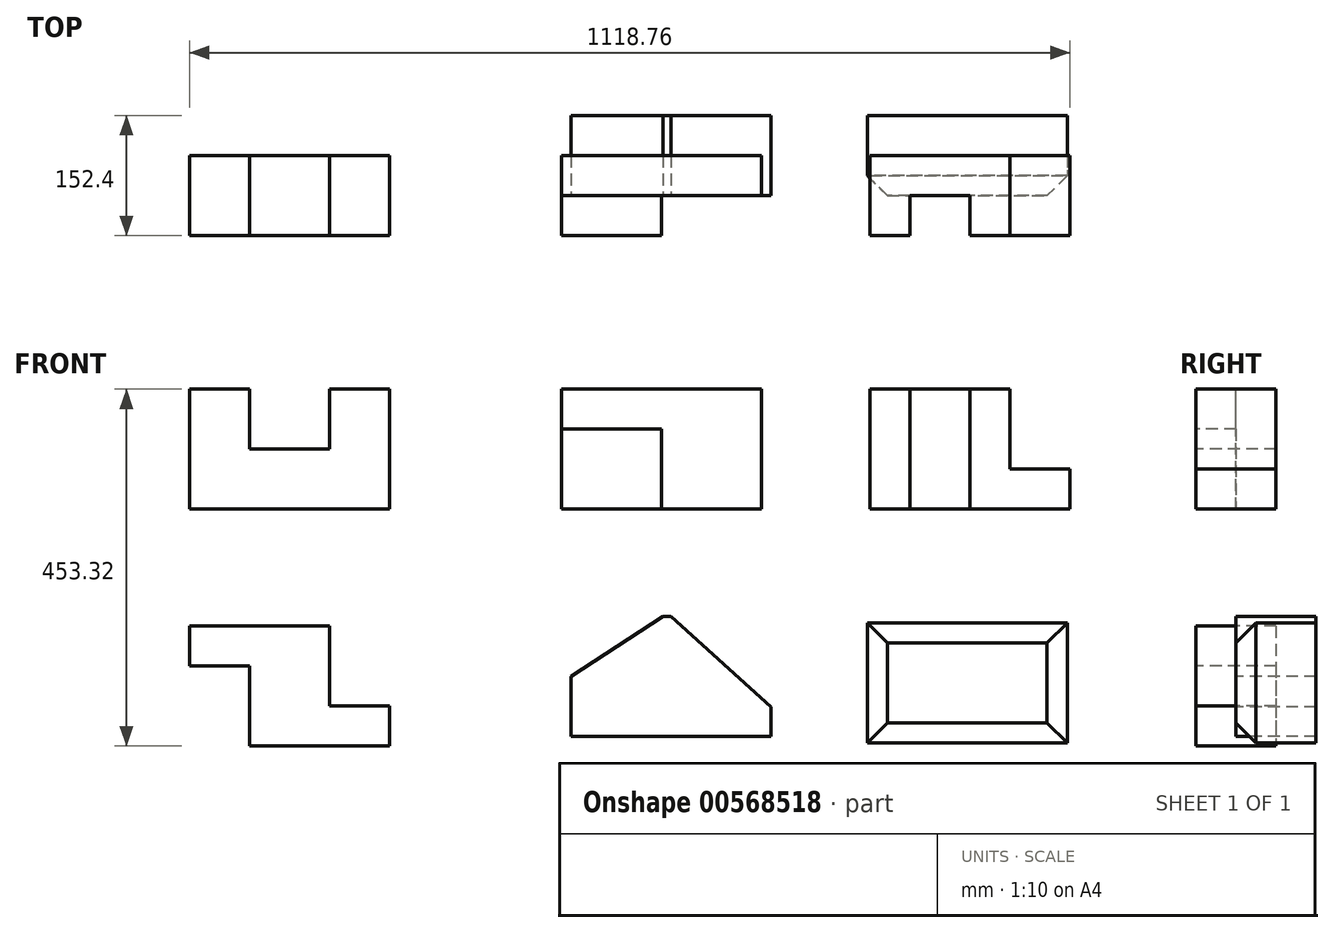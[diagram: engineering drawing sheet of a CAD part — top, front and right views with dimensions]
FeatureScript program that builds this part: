
annotation { "Feature Type Name" : "Feature", "Feature Type Description" : "" }
export const myFeature = defineFeature(function(context is Context, id is Id, definition is map)
    precondition{}
    {
        {
            var Q0;
            Q0=qCreatedBy(makeId("Front.planeOp"),FACE);
            var sketch = newSketch(context, id + "F0", { "sketchPlane" : qUnion([Q0])});
            skLineSegment(sketch, "E0", {"start": v(0, 0) * mm, "end": v(254, 0) * mm});
            skLineSegment(sketch, "E1", {"start": v(254, 0) * mm, "end": v(254, 152.4) * mm});
            skLineSegment(sketch, "E2", {"start": v(254, 152.4) * mm, "end": v(177.8, 152.4) * mm});
            skLineSegment(sketch, "E3", {"start": v(177.8, 152.4) * mm, "end": v(177.8, 76.2) * mm});
            skLineSegment(sketch, "E4", {"start": v(177.8, 76.2) * mm, "end": v(76.2, 76.2) * mm});
            skLineSegment(sketch, "E5", {"start": v(76.2, 76.2) * mm, "end": v(76.2, 152.4) * mm});
            skLineSegment(sketch, "E6", {"start": v(76.2, 152.4) * mm, "end": v(0, 152.4) * mm});
            skLineSegment(sketch, "E7", {"start": v(0, 152.4) * mm, "end": v(0, 0) * mm});
            skSolve(sketch);
        }
        {
            var Q0;
            Q0=makeQuery(id+"F0.imprint","IMPRINT",FACE,{"disambiguationData":[TD([[makeQuery(id+"F0.imprint","IMPRINT",EDGE,{"derivedFrom":sQuery(id+"F0.wireOp",EDGE,"E0")}),1.0]])]});
            extrude(context, id + "F1", {"entities" : qUnion([Q0]), "oppositeDirection" : true, "depth" : 101.6 * mm, "offsetDistance" : 25.4 * mm});
        }
        {
            var Q0;
            Q0=qCreatedBy(makeId("Front.planeOp"),FACE);
            var sketch = newSketch(context, id + "F2", { "sketchPlane" : qUnion([Q0])});
            skLineSegment(sketch, "E8.bottom", {"start": v(472.59, 0) * mm, "end": v(726.59, 0) * mm});
            skLineSegment(sketch, "E8.top", {"start": v(472.59, 152.4) * mm, "end": v(726.59, 152.4) * mm});
            skLineSegment(sketch, "E8.left", {"start": v(472.59, 0) * mm, "end": v(472.59, 152.4) * mm});
            skLineSegment(sketch, "E8.right", {"start": v(726.59, 0) * mm, "end": v(726.59, 152.4) * mm});
            skSolve(sketch);
        }
        {
            var Q0;
            Q0=makeQuery(id+"F2.imprint","IMPRINT",FACE,{"disambiguationData":[TD([[makeQuery(id+"F2.imprint","IMPRINT",EDGE,{"derivedFrom":sQuery(id+"F2.wireOp",EDGE,"E8.bottom")}),1.0]])]});
            extrude(context, id + "F3", {"entities" : qUnion([Q0]), "oppositeDirection" : true, "depth" : 101.6 * mm, "offsetDistance" : 25.4 * mm});
        }
        {
            var Q0;
            Q0=makeQuery(id+"F3.opExtrude","CAP_FACE",FACE,{"disambiguationData":[OSD([sQuery(id+"F2.wireOp",EDGE,"E8.bottom"),sQuery(id+"F2.wireOp",EDGE,"E8.top"),sQuery(id+"F2.wireOp",EDGE,"E8.left"),sQuery(id+"F2.wireOp",EDGE,"E8.right")])],"isStart":true});
            var sketch = newSketch(context, id + "F4", { "sketchPlane" : qUnion([Q0])});
            skLineSegment(sketch, "E9", {"start": v(472.59, 152.4) * mm, "end": v(472.59, 101.6) * mm});
            skLineSegment(sketch, "E10", {"start": v(472.59, 101.6) * mm, "end": v(599.59, 101.6) * mm});
            skLineSegment(sketch, "E11", {"start": v(599.59, 101.6) * mm, "end": v(599.59, 0) * mm});
            skLineSegment(sketch, "E12", {"start": v(472.59, 152.4) * mm, "end": v(726.59, 152.4) * mm});
            skLineSegment(sketch, "E13", {"start": v(726.59, 152.4) * mm, "end": v(726.59, 0) * mm});
            skLineSegment(sketch, "E14", {"start": v(726.59, 0) * mm, "end": v(599.59, 0) * mm});
            skSolve(sketch);
        }
        {
            var Q0;
            Q0=makeQuery(id+"F4.imprint","IMPRINT",FACE,{"disambiguationData":[TD([[makeQuery(id+"F4.imprint","IMPRINT",EDGE,{"derivedFrom":sQuery(id+"F4.wireOp",EDGE,"E9")}),-1.0]])]});
            extrude(context, id + "F5", {"entities" : qUnion([Q0]), "operationType" : NewBodyOperationType.REMOVE, "oppositeDirection" : true, "depth" : 50.8 * mm, "offsetDistance" : 25.4 * mm});
        }
        {
            var Q0;
            Q0=qCreatedBy(makeId("Front.planeOp"),FACE);
            var sketch = newSketch(context, id + "F6", { "sketchPlane" : qUnion([Q0])});
            skLineSegment(sketch, "E15.bottom", {"start": v(864.76, 0) * mm, "end": v(1118.76, 0) * mm});
            skLineSegment(sketch, "E15.top", {"start": v(864.76, 152.4) * mm, "end": v(1118.76, 152.4) * mm});
            skLineSegment(sketch, "E15.left", {"start": v(864.76, 0) * mm, "end": v(864.76, 152.4) * mm});
            skLineSegment(sketch, "E15.right", {"start": v(1118.76, 0) * mm, "end": v(1118.76, 152.4) * mm});
            skSolve(sketch);
        }
        {
            var Q0;
            Q0=makeQuery(id+"F6.imprint","IMPRINT",FACE,{"disambiguationData":[TD([[makeQuery(id+"F6.imprint","IMPRINT",EDGE,{"derivedFrom":sQuery(id+"F6.wireOp",EDGE,"E15.bottom")}),1.0]])]});
            extrude(context, id + "F7", {"entities" : qUnion([Q0]), "oppositeDirection" : true, "depth" : 101.6 * mm, "offsetDistance" : 25.4 * mm});
        }
        {
            var Q0;
            Q0=makeQuery(id+"F7.opExtrude","SWEPT_FACE",FACE,{"disambiguationData":[OSD([sQuery(id+"F6.wireOp",EDGE,"E15.top")])]});
            var sketch = newSketch(context, id + "F8", { "sketchPlane" : qUnion([Q0])});
            skLineSegment(sketch, "E16.bottom", {"start": v(915.56, 0) * mm, "end": v(991.76, 0) * mm});
            skLineSegment(sketch, "E16.top", {"start": v(915.56, 50.8) * mm, "end": v(991.76, 50.8) * mm});
            skLineSegment(sketch, "E16.left", {"start": v(915.56, 0) * mm, "end": v(915.56, 50.8) * mm});
            skLineSegment(sketch, "E16.right", {"start": v(991.76, 0) * mm, "end": v(991.76, 50.8) * mm});
            skSolve(sketch);
        }
        {
            var Q0;
            Q0=makeQuery(id+"F8.imprint","IMPRINT",FACE,{"disambiguationData":[TD([[makeQuery(id+"F8.imprint","IMPRINT",EDGE,{"derivedFrom":sQuery(id+"F8.wireOp",EDGE,"E16.bottom")}),1.0]])]});
            extrude(context, id + "F9", {"entities" : qUnion([Q0]), "operationType" : NewBodyOperationType.REMOVE, "oppositeDirection" : true, "depth" : 152.4 * mm, "offsetDistance" : 25.4 * mm});
        }
        {
            var Q0;
            {var subQ0=sQuery(id+"F6.wireOp",EDGE,"E15.bottom");var subQ1=sQuery(id+"F6.wireOp",EDGE,"E15.right");var subQ2=sQuery(id+"F6.wireOp",EDGE,"E15.top");Q0=makeQuery(id+"F9.boolean.opBoolean","SPLIT",FACE,{"disambiguationData":[TD([makeQuery(id+"F7.opExtrude","SWEPT_FACE",FACE,{"disambiguationData":[OSD([subQ1])]})])],"derivedFrom":makeQuery(id+"F7.opExtrude","CAP_FACE",FACE,{"disambiguationData":[OSD([subQ0,subQ2,sQuery(id+"F6.wireOp",EDGE,"E15.left"),subQ1])],"isStart":true})});}
            var sketch = newSketch(context, id + "F10", { "sketchPlane" : qUnion([Q0])});
            skLineSegment(sketch, "E17.bottom", {"start": v(1042.56, 152.4) * mm, "end": v(1118.76, 152.4) * mm});
            skLineSegment(sketch, "E17.top", {"start": v(1042.56, 50.8) * mm, "end": v(1118.76, 50.8) * mm});
            skLineSegment(sketch, "E17.left", {"start": v(1042.56, 152.4) * mm, "end": v(1042.56, 50.8) * mm});
            skLineSegment(sketch, "E17.right", {"start": v(1118.76, 152.4) * mm, "end": v(1118.76, 50.8) * mm});
            skSolve(sketch);
        }
        {
            var Q0;
            Q0 = qSketchRegion(id + "F10", true);
            extrude(context, id + "F11", {"entities" : qUnion([Q0]), "operationType" : NewBodyOperationType.REMOVE, "oppositeDirection" : true, "depth" : 101.6 * mm, "offsetDistance" : 25.4 * mm});
        }
        {
            var Q0;
            Q0=qCreatedBy(makeId("Front.planeOp"),FACE);
            var sketch = newSketch(context, id + "F12", { "sketchPlane" : qUnion([Q0])});
            skLineSegment(sketch, "E18.bottom", {"start": v(0, -148.52) * mm, "end": v(254, -148.52) * mm});
            skLineSegment(sketch, "E18.top", {"start": v(0, -300.92) * mm, "end": v(254, -300.92) * mm});
            skLineSegment(sketch, "E18.left", {"start": v(0, -148.52) * mm, "end": v(0, -300.92) * mm});
            skLineSegment(sketch, "E18.right", {"start": v(254, -148.52) * mm, "end": v(254, -300.92) * mm});
            skSolve(sketch);
        }
        {
            var Q0;
            Q0=makeQuery(id+"F12.imprint","IMPRINT",FACE,{"disambiguationData":[TD([[makeQuery(id+"F12.imprint","IMPRINT",EDGE,{"derivedFrom":sQuery(id+"F12.wireOp",EDGE,"E18.bottom")}),-1.0]])]});
            extrude(context, id + "F13", {"entities" : qUnion([Q0]), "oppositeDirection" : true, "depth" : 101.6 * mm, "offsetDistance" : 25.4 * mm});
        }
        {
            var Q0;
            Q0=makeQuery(id+"F13.opExtrude","CAP_FACE",FACE,{"disambiguationData":[OSD([sQuery(id+"F12.wireOp",EDGE,"E18.bottom"),sQuery(id+"F12.wireOp",EDGE,"E18.top"),sQuery(id+"F12.wireOp",EDGE,"E18.left"),sQuery(id+"F12.wireOp",EDGE,"E18.right")])],"isStart":true});
            var sketch = newSketch(context, id + "F14", { "sketchPlane" : qUnion([Q0])});
            skLineSegment(sketch, "E19.bottom", {"start": v(0, -199.32) * mm, "end": v(76.2, -199.32) * mm});
            skLineSegment(sketch, "E19.top", {"start": v(0, -300.92) * mm, "end": v(76.2, -300.92) * mm});
            skLineSegment(sketch, "E19.left", {"start": v(0, -199.32) * mm, "end": v(0, -300.92) * mm});
            skLineSegment(sketch, "E19.right", {"start": v(76.2, -199.32) * mm, "end": v(76.2, -300.92) * mm});
            skSolve(sketch);
        }
        {
            var Q0;
            Q0=makeQuery(id+"F14.imprint","IMPRINT",FACE,{"disambiguationData":[TD([[makeQuery(id+"F14.imprint","IMPRINT",EDGE,{"derivedFrom":sQuery(id+"F14.wireOp",EDGE,"E19.bottom")}),-1.0]])]});
            extrude(context, id + "F15", {"entities" : qUnion([Q0]), "operationType" : NewBodyOperationType.REMOVE, "oppositeDirection" : true, "depth" : 101.6 * mm, "offsetDistance" : 25.4 * mm});
        }
        {
            var Q0;
            Q0=makeQuery(id+"F13.opExtrude","CAP_FACE",FACE,{"disambiguationData":[OSD([sQuery(id+"F12.wireOp",EDGE,"E18.bottom"),sQuery(id+"F12.wireOp",EDGE,"E18.top"),sQuery(id+"F12.wireOp",EDGE,"E18.left"),sQuery(id+"F12.wireOp",EDGE,"E18.right")])],"isStart":true});
            var sketch = newSketch(context, id + "F16", { "sketchPlane" : qUnion([Q0])});
            skLineSegment(sketch, "E20.bottom", {"start": v(177.8, -148.52) * mm, "end": v(254, -148.52) * mm});
            skLineSegment(sketch, "E20.top", {"start": v(177.8, -250.12) * mm, "end": v(254, -250.12) * mm});
            skLineSegment(sketch, "E20.left", {"start": v(177.8, -148.52) * mm, "end": v(177.8, -250.12) * mm});
            skLineSegment(sketch, "E20.right", {"start": v(254, -148.52) * mm, "end": v(254, -250.12) * mm});
            skSolve(sketch);
        }
        {
            var Q0;
            Q0=makeQuery(id+"F16.imprint","IMPRINT",FACE,{"disambiguationData":[TD([[makeQuery(id+"F16.imprint","IMPRINT",EDGE,{"derivedFrom":sQuery(id+"F16.wireOp",EDGE,"E20.bottom")}),-1.0]])]});
            extrude(context, id + "F17", {"entities" : qUnion([Q0]), "operationType" : NewBodyOperationType.REMOVE, "oppositeDirection" : true, "depth" : 101.6 * mm, "offsetDistance" : 25.4 * mm});
        }
        {
            var Q0;
            Q0=makeQuery(id+"F5.boolean.opBoolean","COPY",FACE,{"derivedFrom":makeQuery(id+"F5.opExtrude","CAP_FACE",FACE,{"disambiguationData":[OSD([sQuery(id+"F4.wireOp",EDGE,"E9"),sQuery(id+"F4.wireOp",EDGE,"E10"),sQuery(id+"F4.wireOp",EDGE,"E11"),sQuery(id+"F4.wireOp",EDGE,"E12"),sQuery(id+"F4.wireOp",EDGE,"E13"),sQuery(id+"F4.wireOp",EDGE,"E14")])],"isStart":false})});
            var sketch = newSketch(context, id + "F18", { "sketchPlane" : qUnion([Q0])});
            skLineSegment(sketch, "E21.bottom", {"start": v(484.79, -136.23) * mm, "end": v(738.79, -136.23) * mm});
            skLineSegment(sketch, "E21.top", {"start": v(484.79, -288.63) * mm, "end": v(738.79, -288.63) * mm});
            skLineSegment(sketch, "E21.left", {"start": v(484.79, -136.23) * mm, "end": v(484.79, -288.63) * mm});
            skLineSegment(sketch, "E21.right", {"start": v(738.79, -136.23) * mm, "end": v(738.79, -288.63) * mm});
            skSolve(sketch);
        }
        {
            var Q0;
            Q0=makeQuery(id+"F18.imprint","IMPRINT",FACE,{"disambiguationData":[TD([[makeQuery(id+"F18.imprint","IMPRINT",EDGE,{"derivedFrom":sQuery(id+"F18.wireOp",EDGE,"E21.bottom")}),-1.0]])]});
            extrude(context, id + "F19", {"entities" : qUnion([Q0]), "oppositeDirection" : true, "depth" : 101.6 * mm, "offsetDistance" : 25.4 * mm});
        }
        {
            var Q0;
            Q0=makeQuery(id+"F19.opExtrude","CAP_FACE",FACE,{"disambiguationData":[OSD([sQuery(id+"F18.wireOp",EDGE,"E21.bottom"),sQuery(id+"F18.wireOp",EDGE,"E21.top"),sQuery(id+"F18.wireOp",EDGE,"E21.left"),sQuery(id+"F18.wireOp",EDGE,"E21.right")])],"isStart":true});
            var sketch = newSketch(context, id + "F20", { "sketchPlane" : qUnion([Q0])});
            skLineSegment(sketch, "E22", {"start": v(484.79, -212.43) * mm, "end": v(601.87, -136.23) * mm});
            skLineSegment(sketch, "E23", {"start": v(611.79, -136.23) * mm, "end": v(738.79, -251.41) * mm});
            skSolve(sketch);
        }
        {
            var Q0;
            {var subQ0=sQuery(id+"F20.wireOp",EDGE,"E22");Q0=makeQuery(id+"F20.imprint","IMPRINT",FACE,{"disambiguationData":[TD([[makeQuery(id+"F20.imprint","IMPRINT",EDGE,{"derivedFrom":subQ0}),1.0]])]});}
            var Q1;
            {var subQ0=sQuery(id+"F20.wireOp",EDGE,"E23");Q1=makeQuery(id+"F20.imprint","IMPRINT",FACE,{"disambiguationData":[TD([[makeQuery(id+"F20.imprint","IMPRINT",EDGE,{"derivedFrom":subQ0}),1.0]])]});}
            extrude(context, id + "F21", {"entities" : qUnion([Q0, Q1]), "operationType" : NewBodyOperationType.REMOVE, "oppositeDirection" : true, "depth" : 101.6 * mm, "offsetDistance" : 25.4 * mm});
        }
        {
            var Q0;
            Q0=makeQuery(id+"F9.boolean.opBoolean","COPY",FACE,{"derivedFrom":makeQuery(id+"F9.opExtrude","SWEPT_FACE",FACE,{"disambiguationData":[OSD([sQuery(id+"F8.wireOp",EDGE,"E16.top")])]})});
            var sketch = newSketch(context, id + "F22", { "sketchPlane" : qUnion([Q0])});
            skLineSegment(sketch, "E24.bottom", {"start": v(861.03, -144.55) * mm, "end": v(1115.03, -144.55) * mm});
            skLineSegment(sketch, "E24.top", {"start": v(861.03, -296.95) * mm, "end": v(1115.03, -296.95) * mm});
            skLineSegment(sketch, "E24.left", {"start": v(861.03, -144.55) * mm, "end": v(861.03, -296.95) * mm});
            skLineSegment(sketch, "E24.right", {"start": v(1115.03, -144.55) * mm, "end": v(1115.03, -296.95) * mm});
            skSolve(sketch);
        }
        {
            var Q0;
            Q0=makeQuery(id+"F22.imprint","IMPRINT",FACE,{"disambiguationData":[TD([[makeQuery(id+"F22.imprint","IMPRINT",EDGE,{"derivedFrom":sQuery(id+"F22.wireOp",EDGE,"E24.bottom")}),-1.0]])]});
            extrude(context, id + "F23", {"entities" : qUnion([Q0]), "oppositeDirection" : true, "depth" : 101.6 * mm, "offsetDistance" : 25.4 * mm});
        }
        {
            var Q0;
            Q0=makeQuery(id+"F23.opExtrude","CAP_FACE",FACE,{"disambiguationData":[OSD([sQuery(id+"F22.wireOp",EDGE,"E24.bottom"),sQuery(id+"F22.wireOp",EDGE,"E24.top"),sQuery(id+"F22.wireOp",EDGE,"E24.left"),sQuery(id+"F22.wireOp",EDGE,"E24.right")])],"isStart":true});
            chamfer(context, id + "F24", {"entities" : qUnion([Q0]), "width" : 25.4 * mm, "tangentPropagation" : true});
        }
    });
